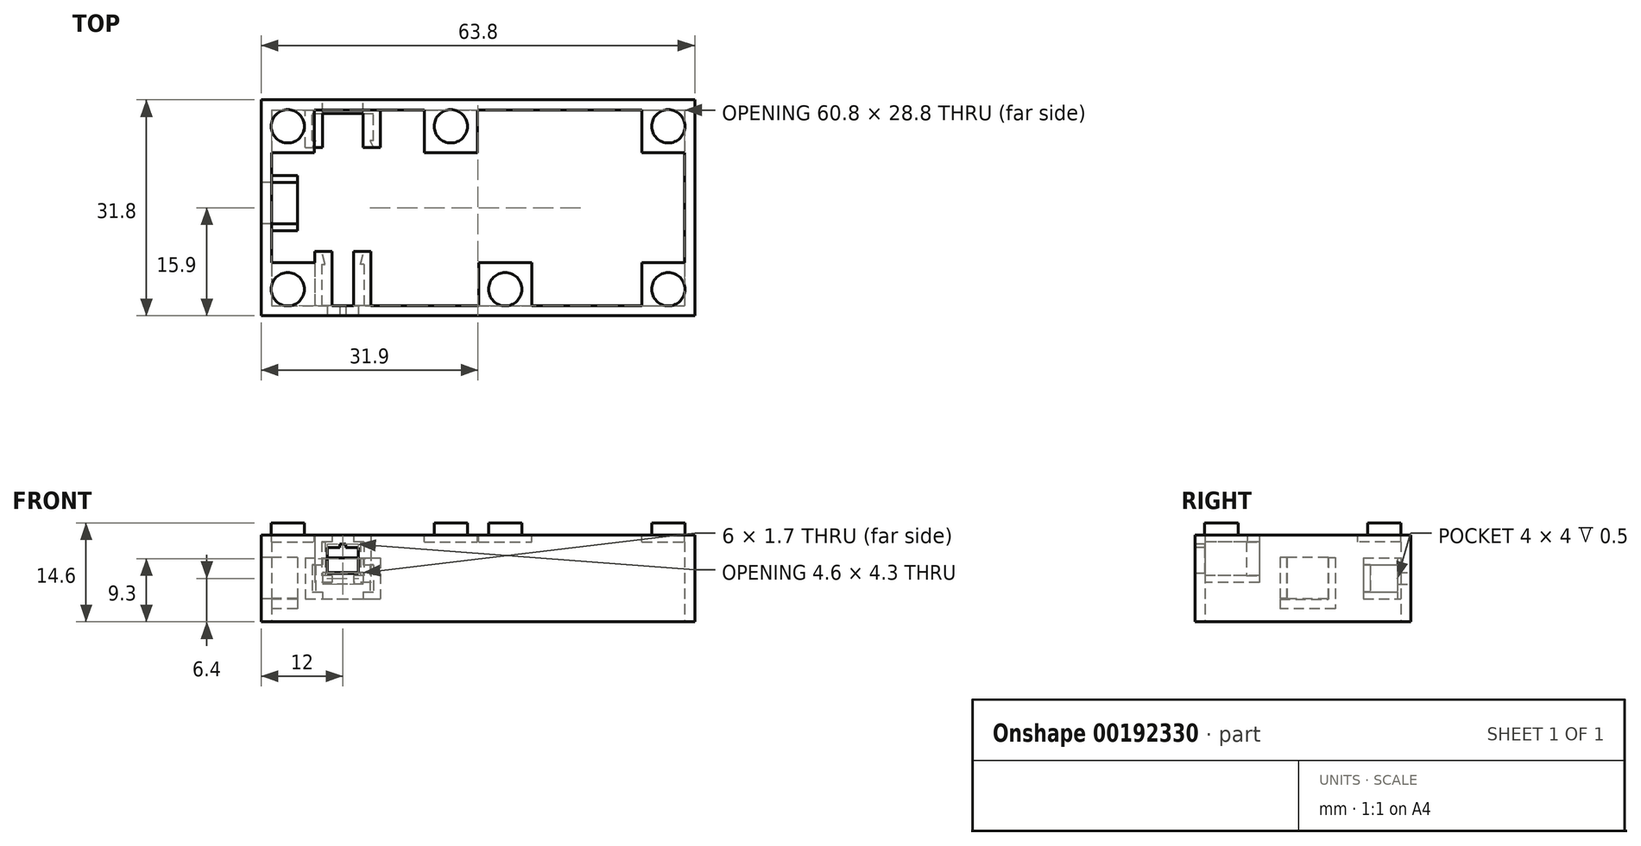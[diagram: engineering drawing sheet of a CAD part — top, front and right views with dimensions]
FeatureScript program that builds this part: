
annotation { "Feature Type Name" : "Feature", "Feature Type Description" : "" }
export const myFeature = defineFeature(function(context is Context, id is Id, definition is map)
    precondition{}
    {
        {
            var Q0;
            Q0=qCreatedBy(makeId("Top.planeOp"),FACE);
            var sketch = newSketch(context, id + "F0", { "sketchPlane" : qUnion([Q0])});
            skLineSegment(sketch, "E0.bottom", {"start": v(0, 31.8) * mm, "end": v(63.8, 31.8) * mm});
            skLineSegment(sketch, "E0.top", {"start": v(0, 0) * mm, "end": v(63.8, 0) * mm});
            skLineSegment(sketch, "E0.left", {"start": v(0, 31.8) * mm, "end": v(0, 0) * mm});
            skLineSegment(sketch, "E0.right", {"start": v(63.8, 31.8) * mm, "end": v(63.8, 0) * mm});
            skPoint(sketch, "E1", {"position": v(31.9, 31.8) * mm});
            skPoint(sketch, "E2", {"position": v(0, 15.9) * mm});
            skLineSegment(sketch, "E3.0", {"start": v(1.5, 30.3) * mm, "end": v(1.5, 1.5) * mm});
            skLineSegment(sketch, "E3.1", {"start": v(1.5, 30.3) * mm, "end": v(62.3, 30.3) * mm});
            skLineSegment(sketch, "E3.2", {"start": v(62.3, 30.3) * mm, "end": v(62.3, 1.5) * mm});
            skLineSegment(sketch, "E3.3", {"start": v(1.5, 1.5) * mm, "end": v(62.3, 1.5) * mm});
            skSolve(sketch);
        }
        {
            var Q0;
            Q0 = qSketchRegion(id + "F0", true);
            extrude(context, id + "F1", {"entities" : qUnion([Q0]), "depth" : 12.8 * mm});
        }
        {
            var Q0;
            Q0=makeQuery(id+"F1.opExtrude","CAP_FACE",FACE,{"disambiguationData":[OSD([sQuery(id+"F0.wireOp",EDGE,"E0.bottom"),sQuery(id+"F0.wireOp",EDGE,"E0.top"),sQuery(id+"F0.wireOp",EDGE,"E0.left"),sQuery(id+"F0.wireOp",EDGE,"E0.right"),sQuery(id+"F0.wireOp",EDGE,"E3.0"),sQuery(id+"F0.wireOp",EDGE,"E3.1"),sQuery(id+"F0.wireOp",EDGE,"E3.2"),sQuery(id+"F0.wireOp",EDGE,"E3.3")])],"isStart":false});
            var sketch = newSketch(context, id + "F2", { "sketchPlane" : qUnion([Q0])});
            skLineSegment(sketch, "E4.bottom", {"start": v(0, 31.8) * mm, "end": v(7.8, 31.8) * mm});
            skLineSegment(sketch, "E4.top", {"start": v(0, 24) * mm, "end": v(7.8, 24) * mm});
            skLineSegment(sketch, "E4.left", {"start": v(0, 31.8) * mm, "end": v(0, 24) * mm});
            skLineSegment(sketch, "E4.right", {"start": v(7.8, 31.8) * mm, "end": v(7.8, 24) * mm});
            skLineSegment(sketch, "E5.bottom", {"start": v(0, 0) * mm, "end": v(7.8, 0) * mm});
            skLineSegment(sketch, "E5.top", {"start": v(0, 7.8) * mm, "end": v(7.8, 7.8) * mm});
            skLineSegment(sketch, "E5.left", {"start": v(0, 0) * mm, "end": v(0, 7.8) * mm});
            skLineSegment(sketch, "E5.right", {"start": v(7.8, 0) * mm, "end": v(7.8, 7.8) * mm});
            skLineSegment(sketch, "E6.bottom", {"start": v(63.8, 31.8) * mm, "end": v(56, 31.8) * mm});
            skLineSegment(sketch, "E6.top", {"start": v(63.8, 24) * mm, "end": v(56, 24) * mm});
            skLineSegment(sketch, "E6.left", {"start": v(63.8, 31.8) * mm, "end": v(63.8, 24) * mm});
            skLineSegment(sketch, "E6.right", {"start": v(56, 31.8) * mm, "end": v(56, 24) * mm});
            skLineSegment(sketch, "E7.bottom", {"start": v(63.8, 0) * mm, "end": v(56, 0) * mm});
            skLineSegment(sketch, "E7.top", {"start": v(63.8, 7.8) * mm, "end": v(56, 7.8) * mm});
            skLineSegment(sketch, "E7.left", {"start": v(63.8, 0) * mm, "end": v(63.8, 7.8) * mm});
            skLineSegment(sketch, "E7.right", {"start": v(56, 0) * mm, "end": v(56, 7.8) * mm});
            skPoint(sketch, "E8.centerSnap0", {"position": v(3.9, 24) * mm});
            skPoint(sketch, "E8.centerSnap1", {"position": v(0, 27.9) * mm});
            skPoint(sketch, "E9.centerSnap0", {"position": v(3.9, 0) * mm});
            skPoint(sketch, "E9.centerSnap1", {"position": v(0, 3.9) * mm});
            skPoint(sketch, "E10.centerSnap0", {"position": v(63.8, 27.9) * mm});
            skPoint(sketch, "E10.centerSnap1", {"position": v(59.9, 31.8) * mm});
            skPoint(sketch, "E11.centerSnap0", {"position": v(59.9, 0) * mm});
            skPoint(sketch, "E11.centerSnap1", {"position": v(63.8, 3.9) * mm});
            skLineSegment(sketch, "E12.bottom", {"start": v(24, 31.8) * mm, "end": v(31.8, 31.8) * mm});
            skLineSegment(sketch, "E12.top", {"start": v(24, 24) * mm, "end": v(31.8, 24) * mm});
            skLineSegment(sketch, "E12.left", {"start": v(24, 31.8) * mm, "end": v(24, 24) * mm});
            skLineSegment(sketch, "E12.right", {"start": v(31.8, 31.8) * mm, "end": v(31.8, 24) * mm});
            skLineSegment(sketch, "E13.bottom", {"start": v(39.8, 0) * mm, "end": v(32, 0) * mm});
            skLineSegment(sketch, "E13.top", {"start": v(39.8, 7.8) * mm, "end": v(32, 7.8) * mm});
            skLineSegment(sketch, "E13.left", {"start": v(39.8, 0) * mm, "end": v(39.8, 7.8) * mm});
            skLineSegment(sketch, "E13.right", {"start": v(32, 0) * mm, "end": v(32, 7.8) * mm});
            skPoint(sketch, "E14", {"position": v(27.9, 31.8) * mm});
            skPoint(sketch, "E15", {"position": v(35.9, 0) * mm});
            skSolve(sketch);
        }
        {
            var Q0;
            {var subQ0=sQuery(id+"F2.wireOp",EDGE,"E4.right");var subQ1=sQuery(id+"F2.wireOp",EDGE,"E4.top");var subQ2=makeQuery(id+"F2.imprint","INTERSECT",VERTEX,{"derivedFrom":[subQ1,subQ0]});Q0=makeQuery(id+"F2.imprint","IMPRINT",FACE,{"disambiguationData":[TD([[makeQuery(id+"F2.imprint","IMPRINT",EDGE,{"disambiguationData":[TD([[subQ2,1.0]])],"derivedFrom":subQ1}),1.0]])]});}
            var Q1;
            {var subQ0=sQuery(id+"F2.wireOp",EDGE,"E5.right");var subQ1=sQuery(id+"F2.wireOp",EDGE,"E5.top");var subQ2=makeQuery(id+"F2.imprint","INTERSECT",VERTEX,{"derivedFrom":[subQ1,subQ0]});Q1=makeQuery(id+"F2.imprint","IMPRINT",FACE,{"disambiguationData":[TD([[makeQuery(id+"F2.imprint","IMPRINT",EDGE,{"disambiguationData":[TD([[subQ2,1.0]])],"derivedFrom":subQ1}),-1.0]])]});}
            var Q2;
            {var subQ0=sQuery(id+"F2.wireOp",EDGE,"E7.right");var subQ1=sQuery(id+"F2.wireOp",EDGE,"E7.top");var subQ2=makeQuery(id+"F2.imprint","INTERSECT",VERTEX,{"derivedFrom":[subQ1,subQ0]});Q2=makeQuery(id+"F2.imprint","IMPRINT",FACE,{"disambiguationData":[TD([[makeQuery(id+"F2.imprint","IMPRINT",EDGE,{"disambiguationData":[TD([[subQ2,1.0]])],"derivedFrom":subQ1}),1.0]])]});}
            var Q3;
            {var subQ0=sQuery(id+"F2.wireOp",EDGE,"E6.right");var subQ1=sQuery(id+"F2.wireOp",EDGE,"E6.top");var subQ2=makeQuery(id+"F2.imprint","INTERSECT",VERTEX,{"derivedFrom":[subQ1,subQ0]});Q3=makeQuery(id+"F2.imprint","IMPRINT",FACE,{"disambiguationData":[TD([[makeQuery(id+"F2.imprint","IMPRINT",EDGE,{"disambiguationData":[TD([[subQ2,1.0]])],"derivedFrom":subQ1}),-1.0]])]});}
            var Q4;
            {var subQ0=sQuery(id+"F2.wireOp",EDGE,"E12.top");Q4=makeQuery(id+"F2.imprint","IMPRINT",FACE,{"disambiguationData":[TD([[makeQuery(id+"F2.imprint","IMPRINT",EDGE,{"derivedFrom":subQ0}),1.0]])]});}
            var Q5;
            {var subQ0=sQuery(id+"F2.wireOp",EDGE,"E13.top");Q5=makeQuery(id+"F2.imprint","IMPRINT",FACE,{"disambiguationData":[TD([[makeQuery(id+"F2.imprint","IMPRINT",EDGE,{"derivedFrom":subQ0}),1.0]])]});}
            extrude(context, id + "F3", {"entities" : qUnion([Q0, Q1, Q2, Q3, Q4, Q5]), "operationType" : NewBodyOperationType.ADD, "oppositeDirection" : true, "depth" : 1 * mm});
        }
        {
            var Q0;
            {var subQ0=sQuery(id+"F0.wireOp",EDGE,"E3.3");var subQ1=sQuery(id+"F0.wireOp",EDGE,"E3.2");var subQ2=sQuery(id+"F0.wireOp",EDGE,"E3.1");var subQ3=sQuery(id+"F0.wireOp",EDGE,"E3.0");Q0=makeQuery(id+"F3.boolean.opBoolean","MERGE",FACE,{"derivedFrom":[makeQuery(id+"F1.opExtrude","CAP_FACE",FACE,{"disambiguationData":[OSD([sQuery(id+"F0.wireOp",EDGE,"E0.bottom"),sQuery(id+"F0.wireOp",EDGE,"E0.top"),sQuery(id+"F0.wireOp",EDGE,"E0.left"),sQuery(id+"F0.wireOp",EDGE,"E0.right"),subQ3,subQ2,subQ1,subQ0])],"isStart":false}),makeQuery(id+"F3.opExtrude","CAP_FACE",FACE,{"disambiguationData":[OSD([subQ3,subQ2,sQuery(id+"F2.wireOp",EDGE,"E4.top"),sQuery(id+"F2.wireOp",EDGE,"E4.right")])],"isStart":true}),makeQuery(id+"F3.opExtrude","CAP_FACE",FACE,{"disambiguationData":[OSD([subQ3,subQ0,sQuery(id+"F2.wireOp",EDGE,"E5.top"),sQuery(id+"F2.wireOp",EDGE,"E5.right")])],"isStart":true}),makeQuery(id+"F3.opExtrude","CAP_FACE",FACE,{"disambiguationData":[OSD([subQ2,subQ1,sQuery(id+"F2.wireOp",EDGE,"E6.top"),sQuery(id+"F2.wireOp",EDGE,"E6.right")])],"isStart":true}),makeQuery(id+"F3.opExtrude","CAP_FACE",FACE,{"disambiguationData":[OSD([subQ1,subQ0,sQuery(id+"F2.wireOp",EDGE,"E7.top"),sQuery(id+"F2.wireOp",EDGE,"E7.right")])],"isStart":true})]});}
            var sketch = newSketch(context, id + "F4", { "sketchPlane" : qUnion([Q0])});
            skLineSegment(sketch, "E16.bottom", {"start": v(0, 31.8) * mm, "end": v(7.8, 31.8) * mm});
            skLineSegment(sketch, "E16.top", {"start": v(0, 24) * mm, "end": v(7.8, 24) * mm});
            skLineSegment(sketch, "E16.left", {"start": v(0, 31.8) * mm, "end": v(0, 24) * mm});
            skLineSegment(sketch, "E16.right", {"start": v(7.8, 31.8) * mm, "end": v(7.8, 24) * mm});
            skLineSegment(sketch, "E17.bottom", {"start": v(0, 0) * mm, "end": v(7.8, 0) * mm});
            skLineSegment(sketch, "E17.top", {"start": v(0, 7.8) * mm, "end": v(7.8, 7.8) * mm});
            skLineSegment(sketch, "E17.left", {"start": v(0, 0) * mm, "end": v(0, 7.8) * mm});
            skLineSegment(sketch, "E17.right", {"start": v(7.8, 0) * mm, "end": v(7.8, 7.8) * mm});
            skLineSegment(sketch, "E18.bottom", {"start": v(63.8, 31.8) * mm, "end": v(56, 31.8) * mm});
            skLineSegment(sketch, "E18.top", {"start": v(63.8, 24) * mm, "end": v(56, 24) * mm});
            skLineSegment(sketch, "E18.left", {"start": v(63.8, 31.8) * mm, "end": v(63.8, 24) * mm});
            skLineSegment(sketch, "E18.right", {"start": v(56, 31.8) * mm, "end": v(56, 24) * mm});
            skLineSegment(sketch, "E19.bottom", {"start": v(63.8, 0) * mm, "end": v(56, 0) * mm});
            skLineSegment(sketch, "E19.top", {"start": v(63.8, 7.8) * mm, "end": v(56, 7.8) * mm});
            skLineSegment(sketch, "E19.left", {"start": v(63.8, 0) * mm, "end": v(63.8, 7.8) * mm});
            skLineSegment(sketch, "E19.right", {"start": v(56, 0) * mm, "end": v(56, 7.8) * mm});
            skCircle(sketch, "E20", {"center": v(3.9, 27.9) * mm, "radius": 2.45 * mm});
            skPoint(sketch, "E20.centerSnap0", {"position": v(3.9, 31.8) * mm});
            skPoint(sketch, "E20.centerSnap1", {"position": v(0, 27.9) * mm});
            skCircle(sketch, "E21", {"center": v(3.9, 3.9) * mm, "radius": 2.45 * mm});
            skPoint(sketch, "E21.centerSnap0", {"position": v(3.9, 0) * mm});
            skPoint(sketch, "E21.centerSnap1", {"position": v(0, 3.9) * mm});
            skCircle(sketch, "E22", {"center": v(59.9, 27.9) * mm, "radius": 2.45 * mm});
            skPoint(sketch, "E22.centerSnap0", {"position": v(63.8, 27.9) * mm});
            skPoint(sketch, "E22.centerSnap1", {"position": v(59.9, 31.8) * mm});
            skCircle(sketch, "E23", {"center": v(59.9, 3.9) * mm, "radius": 2.45 * mm});
            skPoint(sketch, "E23.centerSnap0", {"position": v(59.9, 0) * mm});
            skPoint(sketch, "E23.centerSnap1", {"position": v(63.8, 3.9) * mm});
            skLineSegment(sketch, "E24.bottom", {"start": v(31.8, 24) * mm, "end": v(24, 24) * mm});
            skLineSegment(sketch, "E24.top", {"start": v(31.8, 31.8) * mm, "end": v(24, 31.8) * mm});
            skLineSegment(sketch, "E24.left", {"start": v(31.8, 24) * mm, "end": v(31.8, 31.8) * mm});
            skLineSegment(sketch, "E24.right", {"start": v(24, 24) * mm, "end": v(24, 31.8) * mm});
            skLineSegment(sketch, "E25.bottom", {"start": v(32, 7.8) * mm, "end": v(39.8, 7.8) * mm});
            skLineSegment(sketch, "E25.top", {"start": v(32, 0) * mm, "end": v(39.8, 0) * mm});
            skLineSegment(sketch, "E25.left", {"start": v(32, 7.8) * mm, "end": v(32, 0) * mm});
            skLineSegment(sketch, "E25.right", {"start": v(39.8, 7.8) * mm, "end": v(39.8, 0) * mm});
            skPoint(sketch, "E26", {"position": v(27.9, 31.8) * mm});
            skPoint(sketch, "E27", {"position": v(24, 27.9) * mm});
            skPoint(sketch, "E28", {"position": v(35.9, 7.8) * mm});
            skPoint(sketch, "E29", {"position": v(32, 3.9) * mm});
            skCircle(sketch, "E30", {"center": v(27.9, 27.9) * mm, "radius": 2.45 * mm});
            skCircle(sketch, "E31", {"center": v(35.9, 3.9) * mm, "radius": 2.45 * mm});
            skSolve(sketch);
        }
        {
            var Q0;
            Q0=makeQuery(id+"F4.imprint","IMPRINT",FACE,{"disambiguationData":[TD([[makeQuery(id+"F4.imprint","IMPRINT",EDGE,{"derivedFrom":sQuery(id+"F4.wireOp",EDGE,"E20")}),1.0]])]});
            var Q1;
            Q1=makeQuery(id+"F4.imprint","IMPRINT",FACE,{"disambiguationData":[TD([[makeQuery(id+"F4.imprint","IMPRINT",EDGE,{"derivedFrom":sQuery(id+"F4.wireOp",EDGE,"E22")}),1.0]])]});
            var Q2;
            Q2=makeQuery(id+"F4.imprint","IMPRINT",FACE,{"disambiguationData":[TD([[makeQuery(id+"F4.imprint","IMPRINT",EDGE,{"derivedFrom":sQuery(id+"F4.wireOp",EDGE,"E23")}),1.0]])]});
            var Q3;
            Q3=makeQuery(id+"F4.imprint","IMPRINT",FACE,{"disambiguationData":[TD([[makeQuery(id+"F4.imprint","IMPRINT",EDGE,{"derivedFrom":sQuery(id+"F4.wireOp",EDGE,"E21")}),1.0]])]});
            var Q4;
            Q4=makeQuery(id+"F4.imprint","IMPRINT",FACE,{"disambiguationData":[TD([[makeQuery(id+"F4.imprint","IMPRINT",EDGE,{"derivedFrom":sQuery(id+"F4.wireOp",EDGE,"E30")}),1.0]])]});
            var Q5;
            Q5=makeQuery(id+"F4.imprint","IMPRINT",FACE,{"disambiguationData":[TD([[makeQuery(id+"F4.imprint","IMPRINT",EDGE,{"derivedFrom":sQuery(id+"F4.wireOp",EDGE,"E31")}),1.0]])]});
            extrude(context, id + "F5", {"entities" : qUnion([Q0, Q1, Q2, Q3, Q4, Q5]), "operationType" : NewBodyOperationType.ADD, "depth" : 1.8 * mm});
        }
        {
            var Q0;
            Q0=makeQuery(id+"F1.opExtrude","SWEPT_FACE",FACE,{"disambiguationData":[OSD([sQuery(id+"F0.wireOp",EDGE,"E0.top")])]});
            var sketch = newSketch(context, id + "F6", { "sketchPlane" : qUnion([Q0])});
            skLineSegment(sketch, "E32.bottom", {"start": v(9.7, 10.95) * mm, "end": v(14.3, 10.95) * mm});
            skLineSegment(sketch, "E32.top", {"start": v(9.7, 7.15) * mm, "end": v(14.3, 7.15) * mm});
            skLineSegment(sketch, "E32.left", {"start": v(9.7, 10.95) * mm, "end": v(9.7, 7.15) * mm});
            skLineSegment(sketch, "E32.right", {"start": v(14.3, 10.95) * mm, "end": v(14.3, 7.15) * mm});
            skPoint(sketch, "E33", {"position": v(12, 12.8) * mm});
            skPoint(sketch, "E34", {"position": v(12, 10.95) * mm});
            skLineSegment(sketch, "E35.bottom", {"start": v(11.58, 11.45) * mm, "end": v(12.42, 11.45) * mm});
            skLineSegment(sketch, "E35.top", {"start": v(11.58, 10.95) * mm, "end": v(12.42, 10.95) * mm});
            skLineSegment(sketch, "E35.left", {"start": v(11.58, 11.45) * mm, "end": v(11.58, 10.95) * mm});
            skLineSegment(sketch, "E35.right", {"start": v(12.43, 11.45) * mm, "end": v(12.43, 10.95) * mm});
            skLineSegment(sketch, "E36", {"start": v(12, 11.8) * mm, "end": v(12, 6.8) * mm, "construction": true});
            skPoint(sketch, "E37", {"position": v(12, 9.3) * mm});
            skLineSegment(sketch, "E38", {"start": v(12, 11.45) * mm, "end": v(12, 7.15) * mm, "construction": true});
            skSolve(sketch);
        }
        {
            var Q0;
            Q0=makeQuery(id+"F6.imprint","IMPRINT",FACE,{"disambiguationData":[TD([[makeQuery(id+"F6.imprint","IMPRINT",EDGE,{"derivedFrom":sQuery(id+"F6.wireOp",EDGE,"E32.bottom")}),-1.0]])]});
            var Q1;
            Q1=makeQuery(id+"F6.imprint","IMPRINT",FACE,{"disambiguationData":[TD([[makeQuery(id+"F6.imprint","IMPRINT",EDGE,{"derivedFrom":sQuery(id+"F6.wireOp",EDGE,"b1744aed-7852-425b-a269-eb57eedebe04.bottom")}),-1.0]])]});
            var Q2;
            Q2=makeQuery(id+"F6.imprint","IMPRINT",FACE,{"disambiguationData":[TD([[makeQuery(id+"F6.imprint","IMPRINT",EDGE,{"derivedFrom":sQuery(id+"F6.wireOp",EDGE,"E35.bottom")}),-1.0]])]});
            extrude(context, id + "F7", {"entities" : qUnion([Q0, Q1, Q2]), "operationType" : NewBodyOperationType.REMOVE, "oppositeDirection" : true, "depth" : 25.4 * mm});
        }
        {
            var Q0;
            Q0=makeQuery(id+"F1.opExtrude","SWEPT_FACE",FACE,{"disambiguationData":[OSD([sQuery(id+"F0.wireOp",EDGE,"E3.3")])]});
            var sketch = newSketch(context, id + "F8", { "sketchPlane" : qUnion([Q0])});
            skLineSegment(sketch, "E39.0", {"start": v(-14.3, 7.15) * mm, "end": v(-14.3, 10.95) * mm});
            skLineSegment(sketch, "E40.0", {"start": v(-14.3, 10.95) * mm, "end": v(-12.43, 10.95) * mm});
            skLineSegment(sketch, "E41.0", {"start": v(-12.43, 10.95) * mm, "end": v(-12.43, 11.45) * mm});
            skPoint(sketch, "E42.0", {"position": v(-12, 11.45) * mm});
            skLineSegment(sketch, "E43.0", {"start": v(-12.43, 11.45) * mm, "end": v(-11.58, 11.45) * mm});
            skLineSegment(sketch, "E44.0", {"start": v(-11.58, 10.95) * mm, "end": v(-11.58, 11.45) * mm});
            skLineSegment(sketch, "E45.0", {"start": v(-11.58, 10.95) * mm, "end": v(-9.7, 10.95) * mm});
            skLineSegment(sketch, "E46.0", {"start": v(-9.7, 7.15) * mm, "end": v(-9.7, 10.95) * mm});
            skLineSegment(sketch, "E47.0", {"start": v(-14.3, 7.15) * mm, "end": v(-9.7, 7.15) * mm});
            skLineSegment(sketch, "E48.bottom", {"start": v(-15.1, 11.8) * mm, "end": v(-8.9, 11.8) * mm});
            skLineSegment(sketch, "E48.top", {"start": v(-15.1, 6.8) * mm, "end": v(-8.9, 6.8) * mm});
            skLineSegment(sketch, "E48.left", {"start": v(-15.1, 11.8) * mm, "end": v(-15.1, 6.8) * mm});
            skLineSegment(sketch, "E48.right", {"start": v(-8.9, 11.8) * mm, "end": v(-8.9, 6.8) * mm});
            skPoint(sketch, "E49", {"position": v(-12, 7.15) * mm});
            skPoint(sketch, "E50", {"position": v(-12, 6.8) * mm});
            skLineSegment(sketch, "E51", {"start": v(-12, 11.45) * mm, "end": v(-12, 7.15) * mm, "construction": true});
            skPoint(sketch, "E52", {"position": v(-12, 9.3) * mm});
            skPoint(sketch, "E53", {"position": v(-8.9, 9.3) * mm});
            skLineSegment(sketch, "E54.0", {"start": v(-16.1, 12.8) * mm, "end": v(-7.9, 12.8) * mm});
            skLineSegment(sketch, "E54.1", {"start": v(-16.1, 12.8) * mm, "end": v(-16.1, 5.8) * mm});
            skLineSegment(sketch, "E54.2", {"start": v(-16.1, 5.8) * mm, "end": v(-7.9, 5.8) * mm});
            skLineSegment(sketch, "E54.3", {"start": v(-7.9, 12.8) * mm, "end": v(-7.9, 5.8) * mm});
            skLineSegment(sketch, "E55.bottom", {"start": v(-16.1, 12.8) * mm, "end": v(-13.6, 12.8) * mm});
            skLineSegment(sketch, "E55.top", {"start": v(-16.1, 5.8) * mm, "end": v(-13.6, 5.8) * mm});
            skLineSegment(sketch, "E55.right", {"start": v(-13.6, 12.8) * mm, "end": v(-13.6, 5.8) * mm});
            skLineSegment(sketch, "E56.bottom", {"start": v(-7.9, 12.8) * mm, "end": v(-10.4, 12.8) * mm});
            skLineSegment(sketch, "E56.top", {"start": v(-7.9, 5.8) * mm, "end": v(-10.4, 5.8) * mm});
            skLineSegment(sketch, "E56.right", {"start": v(-10.4, 12.8) * mm, "end": v(-10.4, 5.8) * mm});
            skSolve(sketch);
        }
        {
            var Q0;
            {var subQ1=sQuery(id+"F8.wireOp",EDGE,"E48.left");Q0=makeQuery(id+"F8.imprint","IMPRINT",FACE,{"disambiguationData":[TD([[makeQuery(id+"F8.imprint","IMPRINT",EDGE,{"derivedFrom":subQ1}),-1.0]])]});}
            var Q1;
            {var subQ0=sQuery(id+"F8.wireOp",EDGE,"E48.right");Q1=makeQuery(id+"F8.imprint","IMPRINT",FACE,{"disambiguationData":[TD([[makeQuery(id+"F8.imprint","IMPRINT",EDGE,{"derivedFrom":subQ0}),1.0]])]});}
            extrude(context, id + "F9", {"entities" : qUnion([Q0, Q1]), "operationType" : NewBodyOperationType.ADD, "depth" : 8 * mm});
        }
        {
            var Q0;
            {var subQ0=sQuery(id+"F8.wireOp",EDGE,"E48.top");Q0=makeQuery(id+"F9.opExtrude","SWEPT_FACE",FACE,{"disambiguationData":[OSD([subQ0]),TDD([makeQuery(id+"F8.imprint","IMPRINT",EDGE,{"disambiguationData":[TD([[makeQuery(id+"F8.imprint","INTERSECT",VERTEX,{"derivedFrom":[subQ0,sQuery(id+"F8.wireOp",EDGE,"E48.left")]}),-1.0]])],"derivedFrom":subQ0})])]});}
            var sketch = newSketch(context, id + "F10", { "sketchPlane" : qUnion([Q0])});
            skLineSegment(sketch, "E57", {"start": v(15.1, 7.6) * mm, "end": v(14.6, 7.6) * mm});
            skLineSegment(sketch, "E58", {"start": v(14.6, 7.6) * mm, "end": v(15.1, 9.5) * mm});
            skLineSegment(sketch, "E59.0", {"start": v(8.9, 9.5) * mm, "end": v(8.9, 1.5) * mm});
            skLineSegment(sketch, "E60", {"start": v(8.9, 7.6) * mm, "end": v(9.4, 7.6) * mm});
            skLineSegment(sketch, "E61", {"start": v(9.4, 7.6) * mm, "end": v(8.9, 9.5) * mm});
            skSolve(sketch);
        }
        {
            var Q0;
            {var subQ0=sQuery(id+"F10.wireOp",EDGE,"E57");Q0=makeQuery(id+"F10.imprint","IMPRINT",FACE,{"disambiguationData":[TD([[makeQuery(id+"F10.imprint","IMPRINT",EDGE,{"derivedFrom":subQ0}),-1.0]])]});}
            var Q1;
            {var subQ2=sQuery(id+"F10.wireOp",EDGE,"E60");Q1=makeQuery(id+"F10.imprint","IMPRINT",FACE,{"disambiguationData":[TD([[makeQuery(id+"F10.imprint","IMPRINT",EDGE,{"derivedFrom":subQ2}),1.0]])]});}
            extrude(context, id + "F11", {"entities" : qUnion([Q0, Q1]), "operationType" : NewBodyOperationType.ADD, "endBound" : BoundingType.UP_TO_NEXT, "depth" : 25.4 * mm});
        }
        {
            var Q0;
            Q0=makeQuery(id+"F1.opExtrude","SWEPT_FACE",FACE,{"disambiguationData":[OSD([sQuery(id+"F0.wireOp",EDGE,"E3.3")])]});
            var sketch = newSketch(context, id + "F12", { "sketchPlane" : qUnion([Q0])});
            skLineSegment(sketch, "E62.bottom", {"start": v(-7.9, 12.8) * mm, "end": v(-4.9, 12.8) * mm});
            skLineSegment(sketch, "E62.top", {"start": v(-7.9, 11.8) * mm, "end": v(-4.9, 11.8) * mm});
            skLineSegment(sketch, "E62.left", {"start": v(-7.9, 12.8) * mm, "end": v(-7.9, 11.8) * mm});
            skLineSegment(sketch, "E62.right", {"start": v(-4.9, 12.8) * mm, "end": v(-4.9, 11.8) * mm});
            skSolve(sketch);
        }
        {
            var Q0;
            {var subQ2=sQuery(id+"F12.wireOp",EDGE,"E62.left");Q0=makeQuery(id+"F12.imprint","IMPRINT",FACE,{"disambiguationData":[TD([[makeQuery(id+"F12.imprint","IMPRINT",EDGE,{"derivedFrom":subQ2}),1.0]])]});}
            var Q1;
            Q1=makeQuery(id+"F3.opExtrude","SWEPT_FACE",FACE,{"disambiguationData":[OSD([sQuery(id+"F2.wireOp",EDGE,"E5.top")])]});
            extrude(context, id + "F13", {"entities" : qUnion([Q0]), "operationType" : NewBodyOperationType.ADD, "endBound" : BoundingType.UP_TO_SURFACE, "endBoundEntityFace" : qUnion([Q1]), "depth" : 25.4 * mm});
        }
        {
            var Q0;
            Q0=makeQuery(id+"F1.opExtrude","SWEPT_FACE",FACE,{"disambiguationData":[OSD([sQuery(id+"F0.wireOp",EDGE,"E0.bottom")])]});
            var sketch = newSketch(context, id + "F14", { "sketchPlane" : qUnion([Q0])});
            skLineSegment(sketch, "E63.bottom", {"start": v(-15, 7.25) * mm, "end": v(-9, 7.25) * mm});
            skLineSegment(sketch, "E63.top", {"start": v(-15, 5.55) * mm, "end": v(-9, 5.55) * mm});
            skLineSegment(sketch, "E63.left", {"start": v(-15, 7.25) * mm, "end": v(-15, 5.55) * mm});
            skLineSegment(sketch, "E63.right", {"start": v(-9, 7.25) * mm, "end": v(-9, 5.55) * mm});
            skPoint(sketch, "E64", {"position": v(0, 6.4) * mm});
            skPoint(sketch, "E65", {"position": v(-9, 6.4) * mm});
            skPoint(sketch, "E66", {"position": v(-12, 7.25) * mm});
            skSolve(sketch);
        }
        {
            var Q0;
            Q0=makeQuery(id+"F14.imprint","IMPRINT",FACE,{"disambiguationData":[TD([[makeQuery(id+"F14.imprint","IMPRINT",EDGE,{"derivedFrom":sQuery(id+"F14.wireOp",EDGE,"E63.bottom")}),-1.0]])]});
            extrude(context, id + "F15", {"entities" : qUnion([Q0]), "operationType" : NewBodyOperationType.REMOVE, "oppositeDirection" : true, "depth" : 2.54 * mm});
        }
        {
            var Q0;
            Q0=makeQuery(id+"F1.opExtrude","SWEPT_FACE",FACE,{"disambiguationData":[OSD([sQuery(id+"F0.wireOp",EDGE,"E3.1")])]});
            var sketch = newSketch(context, id + "F16", { "sketchPlane" : qUnion([Q0])});
            skLineSegment(sketch, "E67.bottom", {"start": v(6.5, 9.4) * mm, "end": v(17.5, 9.4) * mm});
            skLineSegment(sketch, "E67.top", {"start": v(6.5, 3.4) * mm, "end": v(17.5, 3.4) * mm});
            skLineSegment(sketch, "E67.left", {"start": v(6.5, 9.4) * mm, "end": v(6.5, 3.4) * mm});
            skLineSegment(sketch, "E67.right", {"start": v(17.5, 9.4) * mm, "end": v(17.5, 3.4) * mm});
            skPoint(sketch, "E68", {"position": v(12, 9.4) * mm});
            skPoint(sketch, "E69", {"position": v(12, 7.25) * mm});
            skPoint(sketch, "E70", {"position": v(15, 6.4) * mm});
            skPoint(sketch, "E71", {"position": v(17.5, 6.4) * mm});
            skSolve(sketch);
        }
        {
            var Q0;
            Q0=makeQuery(id+"F16.imprint","IMPRINT",FACE,{"disambiguationData":[TD([[makeQuery(id+"F16.imprint","IMPRINT",EDGE,{"derivedFrom":sQuery(id+"F16.wireOp",EDGE,"E67.bottom")}),-1.0]])]});
            extrude(context, id + "F17", {"entities" : qUnion([Q0]), "operationType" : NewBodyOperationType.ADD, "depth" : .5 * mm});
        }
        {
            var Q0;
            Q0=makeQuery(id+"F17.opExtrude","CAP_FACE",FACE,{"disambiguationData":[OSD([sQuery(id+"F0.wireOp",EDGE,"E3.1"),sQuery(id+"F14.wireOp",EDGE,"E63.bottom"),sQuery(id+"F14.wireOp",EDGE,"E63.top"),sQuery(id+"F14.wireOp",EDGE,"E63.left"),sQuery(id+"F14.wireOp",EDGE,"E63.right"),sQuery(id+"F16.wireOp",EDGE,"E67.bottom"),sQuery(id+"F16.wireOp",EDGE,"E67.top"),sQuery(id+"F16.wireOp",EDGE,"E67.left"),sQuery(id+"F16.wireOp",EDGE,"E67.right")])],"isStart":false});
            var sketch = newSketch(context, id + "F18", { "sketchPlane" : qUnion([Q0])});
            skLineSegment(sketch, "E72.0", {"start": v(6.5, 9.4) * mm, "end": v(6.5, 3.4) * mm});
            skLineSegment(sketch, "E72.1", {"start": v(6.5, 9.4) * mm, "end": v(17.5, 9.4) * mm});
            skLineSegment(sketch, "E72.2", {"start": v(17.5, 9.4) * mm, "end": v(17.5, 3.4) * mm});
            skLineSegment(sketch, "E72.3", {"start": v(6.5, 3.4) * mm, "end": v(17.5, 3.4) * mm});
            skLineSegment(sketch, "E73.bottom", {"start": v(7.5, 8.4) * mm, "end": v(16.5, 8.4) * mm});
            skLineSegment(sketch, "E73.top", {"start": v(7.5, 4.4) * mm, "end": v(16.5, 4.4) * mm});
            skLineSegment(sketch, "E73.left", {"start": v(7.5, 8.4) * mm, "end": v(7.5, 4.4) * mm});
            skLineSegment(sketch, "E73.right", {"start": v(16.5, 8.4) * mm, "end": v(16.5, 4.4) * mm});
            skPoint(sketch, "E74", {"position": v(12, 8.4) * mm});
            skPoint(sketch, "E75", {"position": v(12, 9.4) * mm});
            skPoint(sketch, "E76", {"position": v(16.5, 6.4) * mm});
            skPoint(sketch, "E77", {"position": v(17.5, 6.4) * mm});
            skLineSegment(sketch, "E78.bottom", {"start": v(17.5, 9.4) * mm, "end": v(15, 9.4) * mm});
            skLineSegment(sketch, "E78.top", {"start": v(17.5, 3.4) * mm, "end": v(15, 3.4) * mm});
            skLineSegment(sketch, "E78.right", {"start": v(15, 9.4) * mm, "end": v(15, 3.4) * mm});
            skLineSegment(sketch, "E79.bottom", {"start": v(6.5, 9.4) * mm, "end": v(9, 9.4) * mm});
            skLineSegment(sketch, "E79.top", {"start": v(6.5, 3.4) * mm, "end": v(9, 3.4) * mm});
            skLineSegment(sketch, "E79.right", {"start": v(9, 9.4) * mm, "end": v(9, 3.4) * mm});
            skSolve(sketch);
        }
        {
            var Q0;
            {var subQ1=sQuery(id+"F18.wireOp",EDGE,"E73.left");Q0=makeQuery(id+"F18.imprint","IMPRINT",FACE,{"disambiguationData":[TD([[makeQuery(id+"F18.imprint","IMPRINT",EDGE,{"derivedFrom":subQ1}),-1.0]])]});}
            var Q1;
            {var subQ1=sQuery(id+"F18.wireOp",EDGE,"E73.right");Q1=makeQuery(id+"F18.imprint","IMPRINT",FACE,{"disambiguationData":[TD([[makeQuery(id+"F18.imprint","IMPRINT",EDGE,{"derivedFrom":subQ1}),1.0]])]});}
            extrude(context, id + "F19", {"entities" : qUnion([Q0, Q1]), "operationType" : NewBodyOperationType.ADD, "depth" : 5 * mm});
        }
        {
            var Q0;
            {var subQ0=sQuery(id+"F18.wireOp",EDGE,"E73.top");Q0=makeQuery(id+"F19.opExtrude","SWEPT_FACE",FACE,{"disambiguationData":[OSD([subQ0]),TDD([makeQuery(id+"F18.imprint","IMPRINT",EDGE,{"disambiguationData":[TD([[makeQuery(id+"F18.imprint","INTERSECT",VERTEX,{"derivedFrom":[subQ0,sQuery(id+"F18.wireOp",EDGE,"E73.left")]}),-1.0]])],"derivedFrom":subQ0})])]});}
            var sketch = newSketch(context, id + "F20", { "sketchPlane" : qUnion([Q0])});
            skLineSegment(sketch, "E80.0", {"start": v(7.5, 24.8) * mm, "end": v(7.5, 29.8) * mm});
            skLineSegment(sketch, "E80.1", {"start": v(16.5, 24.8) * mm, "end": v(16.5, 29.8) * mm});
            skLineSegment(sketch, "E81", {"start": v(16.5, 25.8) * mm, "end": v(16, 25.8) * mm});
            skLineSegment(sketch, "E82", {"start": v(16, 25.8) * mm, "end": v(16.5, 24.8) * mm});
            skLineSegment(sketch, "E83", {"start": v(7.5, 25.8) * mm, "end": v(8, 25.8) * mm});
            skLineSegment(sketch, "E84", {"start": v(8, 25.8) * mm, "end": v(7.5, 24.8) * mm});
            skSolve(sketch);
        }
        {
            var Q0;
            {var subQ3=sQuery(id+"F20.wireOp",EDGE,"E83");Q0=makeQuery(id+"F20.imprint","IMPRINT",FACE,{"disambiguationData":[TD([[makeQuery(id+"F20.imprint","IMPRINT",EDGE,{"derivedFrom":subQ3}),-1.0]])]});}
            var Q1;
            {var subQ2=sQuery(id+"F20.wireOp",EDGE,"E81");Q1=makeQuery(id+"F20.imprint","IMPRINT",FACE,{"disambiguationData":[TD([[makeQuery(id+"F20.imprint","IMPRINT",EDGE,{"derivedFrom":subQ2}),1.0]])]});}
            extrude(context, id + "F21", {"entities" : qUnion([Q0, Q1]), "operationType" : NewBodyOperationType.ADD, "endBound" : BoundingType.UP_TO_NEXT, "depth" : 25.4 * mm});
        }
        {
            var Q0;
            Q0=makeQuery(id+"F1.opExtrude","SWEPT_FACE",FACE,{"disambiguationData":[OSD([sQuery(id+"F0.wireOp",EDGE,"E0.left")])]});
            var sketch = newSketch(context, id + "F22", { "sketchPlane" : qUnion([Q0])});
            skLineSegment(sketch, "E85.bottom", {"start": v(-13.54, 3.4) * mm, "end": v(-19.64, 3.4) * mm});
            skLineSegment(sketch, "E85.top", {"start": v(-13.54, 9.5) * mm, "end": v(-19.64, 9.5) * mm});
            skLineSegment(sketch, "E85.left", {"start": v(-13.54, 3.4) * mm, "end": v(-13.54, 9.5) * mm});
            skLineSegment(sketch, "E85.right", {"start": v(-19.64, 3.4) * mm, "end": v(-19.64, 9.5) * mm});
            skSolve(sketch);
        }
        {
            var Q0;
            Q0=makeQuery(id+"F22.imprint","IMPRINT",FACE,{"disambiguationData":[TD([[makeQuery(id+"F22.imprint","IMPRINT",EDGE,{"derivedFrom":sQuery(id+"F22.wireOp",EDGE,"E85.bottom")}),-1.0]])]});
            extrude(context, id + "F23", {"entities" : qUnion([Q0]), "operationType" : NewBodyOperationType.REMOVE, "oppositeDirection" : true, "depth" : 25.4 * mm});
        }
        {
            var Q0;
            Q0=makeQuery(id+"F1.opExtrude","SWEPT_FACE",FACE,{"disambiguationData":[OSD([sQuery(id+"F0.wireOp",EDGE,"E3.0")])]});
            var sketch = newSketch(context, id + "F24", { "sketchPlane" : qUnion([Q0])});
            skLineSegment(sketch, "E86.bottom", {"start": v(13.54, 9.5) * mm, "end": v(12.51, 9.5) * mm});
            skLineSegment(sketch, "E86.top", {"start": v(13.54, 3.43) * mm, "end": v(12.51, 3.43) * mm});
            skLineSegment(sketch, "E86.left", {"start": v(13.54, 9.5) * mm, "end": v(13.54, 3.43) * mm});
            skLineSegment(sketch, "E86.right", {"start": v(12.51, 9.5) * mm, "end": v(12.51, 3.43) * mm});
            skSolve(sketch);
        }
        {
            var Q0;
            Q0 = qSketchRegion(id + "F24", true);
            extrude(context, id + "F25", {"entities" : qUnion([Q0]), "operationType" : NewBodyOperationType.ADD, "depth" : 3.8 * mm});
        }
        {
            var Q0;
            Q0=makeQuery(id+"F1.opExtrude","SWEPT_FACE",FACE,{"disambiguationData":[OSD([sQuery(id+"F0.wireOp",EDGE,"E3.0")])]});
            var sketch = newSketch(context, id + "F26", { "sketchPlane" : qUnion([Q0])});
            skLineSegment(sketch, "E87.bottom", {"start": v(19.64, 9.5) * mm, "end": v(20.66, 9.5) * mm});
            skLineSegment(sketch, "E87.top", {"start": v(19.64, 3.31) * mm, "end": v(20.66, 3.31) * mm});
            skLineSegment(sketch, "E87.left", {"start": v(19.64, 9.5) * mm, "end": v(19.64, 3.31) * mm});
            skLineSegment(sketch, "E87.right", {"start": v(20.66, 9.5) * mm, "end": v(20.66, 3.31) * mm});
            skSolve(sketch);
        }
        {
            var Q0;
            Q0 = qSketchRegion(id + "F26", true);
            extrude(context, id + "F27", {"entities" : qUnion([Q0]), "operationType" : NewBodyOperationType.ADD, "depth" : 3.8 * mm});
        }
        {
            var Q0;
            Q0=makeQuery(id+"F1.opExtrude","SWEPT_FACE",FACE,{"disambiguationData":[OSD([sQuery(id+"F0.wireOp",EDGE,"E3.0")])]});
            var sketch = newSketch(context, id + "F28", { "sketchPlane" : qUnion([Q0])});
            skLineSegment(sketch, "E88.bottom", {"start": v(20.66, 3.31) * mm, "end": v(12.5, 3.31) * mm});
            skLineSegment(sketch, "E88.top", {"start": v(20.66, 1.92) * mm, "end": v(12.5, 1.92) * mm});
            skLineSegment(sketch, "E88.left", {"start": v(20.66, 3.31) * mm, "end": v(20.66, 1.92) * mm});
            skLineSegment(sketch, "E88.right", {"start": v(12.5, 3.31) * mm, "end": v(12.5, 1.92) * mm});
            skSolve(sketch);
        }
        {
            var Q0;
            Q0 = qSketchRegion(id + "F28", true);
            extrude(context, id + "F29", {"entities" : qUnion([Q0]), "operationType" : NewBodyOperationType.ADD, "depth" : 3.8 * mm});
        }
    });
